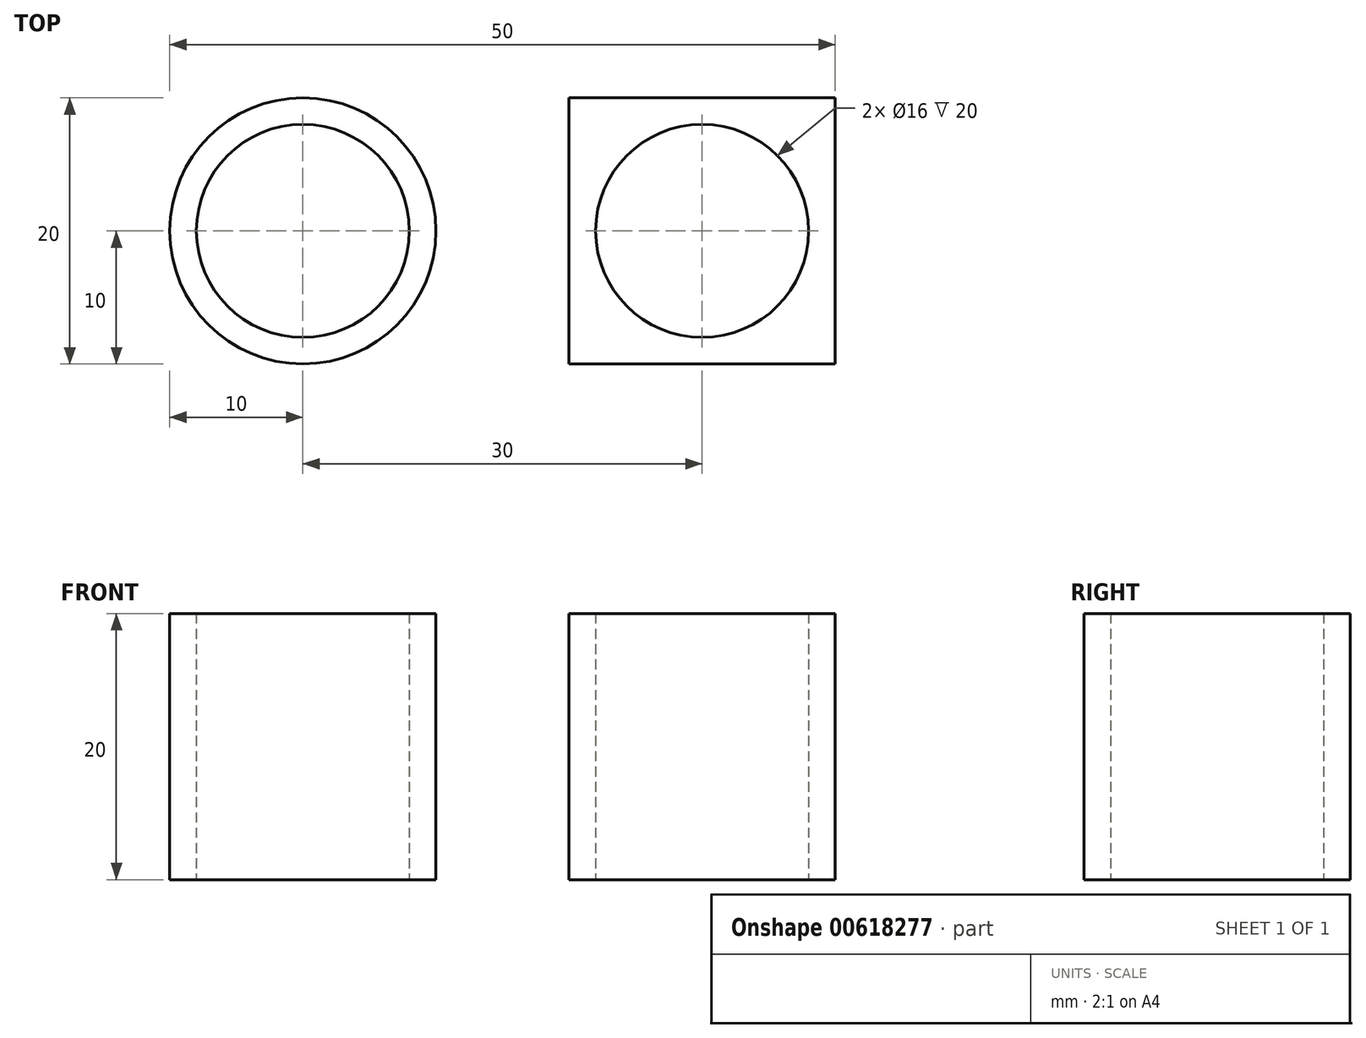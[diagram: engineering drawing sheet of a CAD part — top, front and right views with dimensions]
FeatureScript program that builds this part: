
annotation { "Feature Type Name" : "Feature", "Feature Type Description" : "" }
export const myFeature = defineFeature(function(context is Context, id is Id, definition is map)
    precondition{}
    {
        {
            var Q0;
            Q0=qCreatedBy(makeId("Top.planeOp"),FACE);
            var sketch = newSketch(context, id + "F0", { "sketchPlane" : qUnion([Q0])});
            skCircle(sketch, "E0", {"center": v(0, 0) * mm, "radius": 10 * mm});
            skCircle(sketch, "E1", {"center": v(0, 0) * mm, "radius": 8 * mm});
            skCircle(sketch, "E2", {"center": v(30, 0) * mm, "radius": 8 * mm});
            skLineSegment(sketch, "E3.bottom", {"start": v(40, 10) * mm, "end": v(20, 10) * mm});
            skLineSegment(sketch, "E3.top", {"start": v(40, -10) * mm, "end": v(20, -10) * mm});
            skLineSegment(sketch, "E3.left", {"start": v(40, 10) * mm, "end": v(40, -10) * mm});
            skLineSegment(sketch, "E3.right", {"start": v(20, 10) * mm, "end": v(20, -10) * mm});
            skSolve(sketch);
        }
        {
            var Q0;
            Q0=makeQuery(id+"F0.imprint","IMPRINT",FACE,{"disambiguationData":[TD([[makeQuery(id+"F0.imprint","IMPRINT",EDGE,{"derivedFrom":sQuery(id+"F0.wireOp",EDGE,"E0")}),1.0]])]});
            var Q1;
            Q1=makeQuery(id+"F0.imprint","IMPRINT",FACE,{"disambiguationData":[TD([[makeQuery(id+"F0.imprint","IMPRINT",EDGE,{"derivedFrom":sQuery(id+"F0.wireOp",EDGE,"E2")}),-1.0]])]});
            extrude(context, id + "F1", {"entities" : qUnion([Q0, Q1]), "depth" : 20 * mm, "offsetDistance" : 25 * mm});
        }
    });
